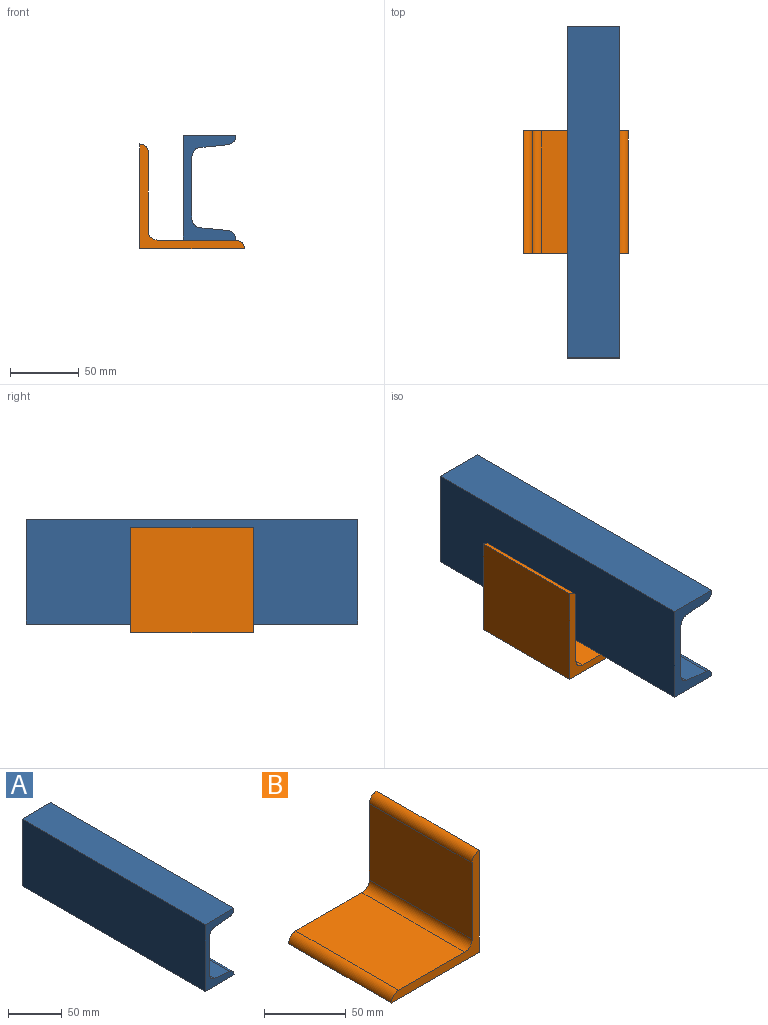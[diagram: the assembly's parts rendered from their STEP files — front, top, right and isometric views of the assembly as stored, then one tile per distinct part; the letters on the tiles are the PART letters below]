
ASSEMBLY  parts=2 mates=1
PART A: 14 faces, bbox 38.1x241.3x76.2 mm
  f0: cylinder r=6.35mm len=241.3mm, axis (0,1,0), area 2254.1mm2, adj f1,f11,f12,f13
  f1: plane 241.3x45.66mm, normal (1,0,0), area 11017mm2, adj f0,f2,f12,f13
  f2: cylinder r=6.35mm len=241.3mm, axis (0,1,0), area 2254.1mm2, adj f1,f3,f12,f13
  f3: plane 241.3x20.31mm, normal (0.1,0,-1), area 4926.1mm2, adj f2,f4,f12,f13
  f4: cylinder r=6.35mm len=241.3mm, axis (0,1,0), area 2254.1mm2, adj f3,f5,f12,f13
  f5: plane 241.3x0.6mm, normal (1,0,0), area 145.6mm2, adj f4,f6,f12,f13
  f6: plane 241.3x38.1mm, normal (0,0,1), area 9193.5mm2, adj f5,f7,f12,f13
  f7: plane 241.3x76.2mm, normal (-1,0,0), area 18387.1mm2, adj f6,f8,f12,f13
  f8: plane 241.3x38.1mm, normal (0,0,-1), area 9193.5mm2, adj f7,f9,f12,f13
  f9: plane 241.3x0.6mm, normal (1,0,0), area 145.6mm2, adj f8,f10,f12,f13
  f10: cylinder r=6.35mm len=241.3mm, axis (0,1,0), area 2254.1mm2, adj f9,f11,f12,f13
  f11: plane 241.3x20.31mm, normal (0.1,0,1), area 4926.1mm2, adj f0,f10,f12,f13
  f12: plane 76.2x38.1mm, normal (0,-1,0), area 987.9mm2, adj f0,f1,f2,f3,f4,f5,f6,f7
  f13: plane 76.2x38.1mm, normal (0,1,0), area 987.9mm2, adj f0,f1,f2,f3,f4,f5,f6,f7
PART B: 9 faces, bbox 76.2x88.9x76.2 mm
  f0: cylinder r=6.35mm len=88.9mm, axis (0,1,0), area 886.7mm2, adj f1,f6,f7,f8
  f1: plane 88.9x57.15mm, normal (0,0,1), area 5080.6mm2, adj f0,f2,f7,f8
  f2: cylinder r=6.35mm len=88.9mm, axis (0,1,0), area 886.7mm2, adj f1,f3,f7,f8
  f3: plane 88.9x76.2mm, normal (0,0,-1), area 6774.2mm2, adj f2,f4,f7,f8
  f4: plane 88.9x76.2mm, normal (1,0,0), area 6774.2mm2, adj f3,f5,f7,f8
  f5: cylinder r=6.35mm len=88.9mm, axis (0,1,0), area 886.7mm2, adj f4,f6,f7,f8
  f6: plane 88.9x57.15mm, normal (-1,0,0), area 5080.6mm2, adj f0,f5,f7,f8
  f7: plane 76.2x76.2mm, normal (0,-1,0), area 918.8mm2, adj f0,f1,f2,f3,f4,f5,f6
  f8: plane 76.2x76.2mm, normal (0,1,0), area 918.8mm2, adj f0,f1,f2,f3,f4,f5,f6
PLACE A t=(-11.68,-2.85,-4.45)mm
PLACE B rot(axis=(0,1,0),90deg) t=(-46.51,-2.85,-52.44)mm
MATE fastened B.f6 <-> A.f8  axis (0,0,1) through (23.34,-2.85,-46.09)mm
